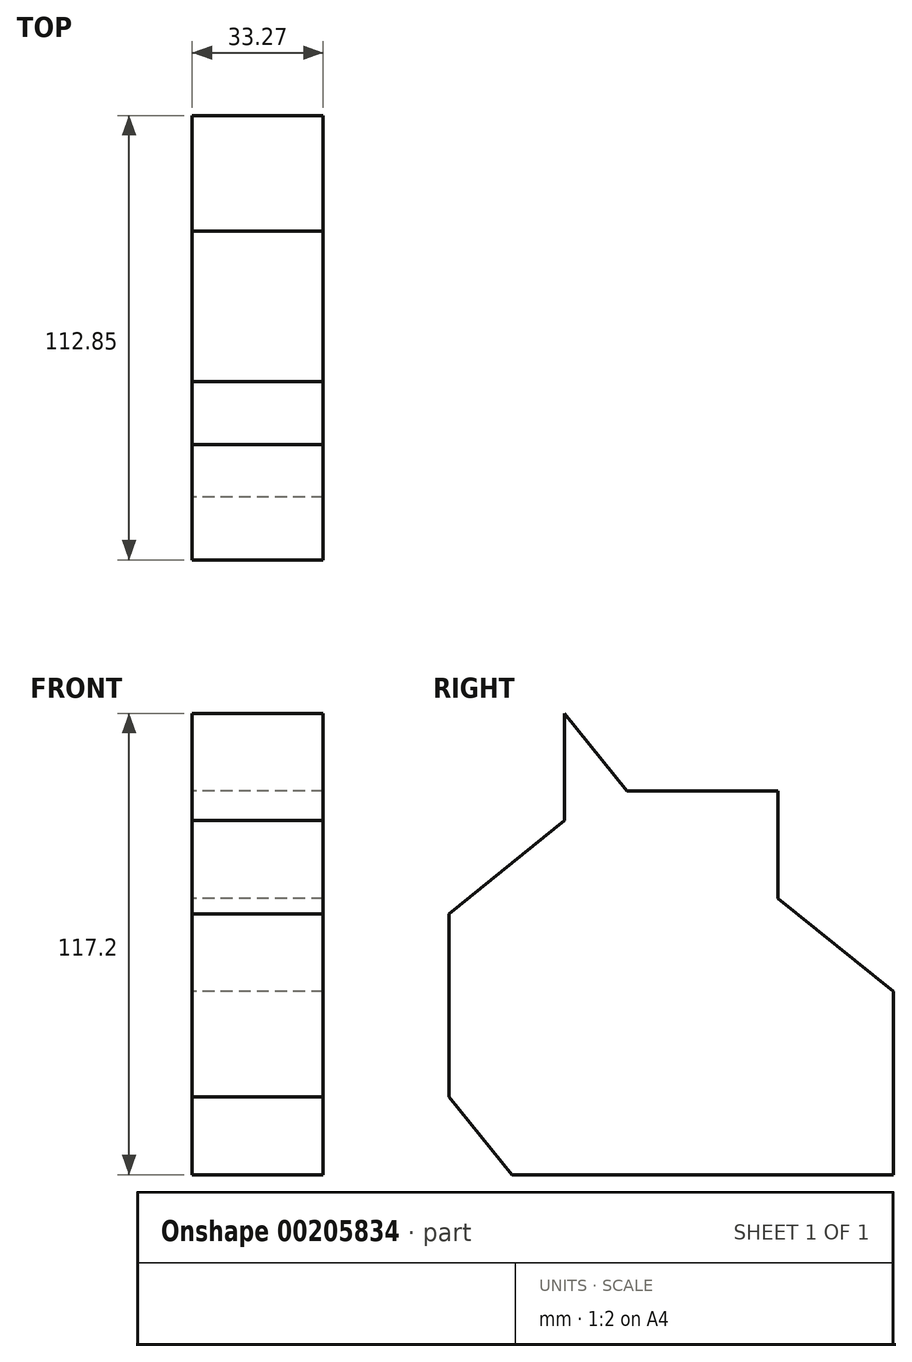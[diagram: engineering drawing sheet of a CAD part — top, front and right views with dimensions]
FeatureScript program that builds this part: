
annotation { "Feature Type Name" : "Feature", "Feature Type Description" : "" }
export const myFeature = defineFeature(function(context is Context, id is Id, definition is map)
    precondition{}
    {
        {
            var Q0;
            Q0=qCreatedBy(makeId("Right.planeOp"),FACE);
            var sketch = newSketch(context, id + "F0", { "sketchPlane" : qUnion([Q0])});
            skLineSegment(sketch, "E0", {"start": v(-19.17, 50.95) * mm, "end": v(-19.17, 23.71) * mm});
            skLineSegment(sketch, "E1", {"start": v(-19.17, 23.71) * mm, "end": v(-48.43, 0) * mm});
            skLineSegment(sketch, "E2", {"start": v(-48.43, 0) * mm, "end": v(-48.43, -46.51) * mm});
            skLineSegment(sketch, "E3", {"start": v(-48.43, -46.51) * mm, "end": v(0, -46.51) * mm});
            skLineSegment(sketch, "E4", {"start": v(-19.17, 50.95) * mm, "end": v(0, 50.95) * mm});
            skLineSegment(sketch, "E5.MirrorCS", {"start": v(19.17, 50.95) * mm, "end": v(0, 50.95) * mm});
            skLineSegment(sketch, "E6.MirrorCS", {"start": v(19.17, 50.95) * mm, "end": v(19.17, 23.71) * mm});
            skLineSegment(sketch, "E7.MirrorCS", {"start": v(19.17, 23.71) * mm, "end": v(48.43, 0) * mm});
            skLineSegment(sketch, "E8.MirrorCS", {"start": v(48.43, 0) * mm, "end": v(48.43, -46.51) * mm});
            skLineSegment(sketch, "E9.MirrorCS", {"start": v(48.43, -46.51) * mm, "end": v(0, -46.51) * mm});
            skSolve(sketch);
        }
        {
            var Q0;
            Q0 = qSketchRegion(id + "F0", true);
            extrude(context, id + "F1", {"entities" : qUnion([Q0]), "depth" : 33.27 * mm});
        }
        {
            var Q0;
            Q0=makeQuery(id+"F1.opExtrude","SWEPT_FACE",FACE,{"disambiguationData":[OSD([sQuery(id+"F0.wireOp",EDGE,"E1")])]});
            var Q1;
            Q1=makeQuery(id+"F1.opExtrude","SWEPT_FACE",FACE,{"disambiguationData":[OSD([sQuery(id+"F0.wireOp",EDGE,"E2")])]});
            var Q2;
            Q2=makeQuery(id+"F1.opExtrude","SWEPT_FACE",FACE,{"disambiguationData":[OSD([sQuery(id+"F0.wireOp",EDGE,"E0")])]});
            extrude(context, id + "F2", {"entities" : qUnion([Q0, Q1, Q2]), "operationType" : NewBodyOperationType.ADD, "depth" : 25.4 * mm});
        }
    });
